# Revit family: MAGIC-HUBLOT_16W_DETECTEUR_1500LM
name_source: partatom
category: Lighting Fixtures
units: mm (PartAtom-declared; Revit-internal decimal feet)

## family parameters
Always vertical = Yes
Cut with Voids When Loaded = No
Host = Ceiling
Light Source = Yes
OmniClass Number = 23.80.70.11
OmniClass Title = Luminaries for Internal Lighting
Part Type = Normal
Room Calculation Point = No
Round Connector Dimension = Use Diameter
Shared = No

## types (1)
- Type 1
    Alimentation = AC 220-240V
    Champs de détection = 180°/360°
    Color Filter = 16777215
    Default Elevation = 0 mm  [stored 0 ft]
    Dimensions = Ø265 x 40 mm
    Dimming Lamp Color Temperature Shift = <None>
    Distance de détection = Mur : 5 à 15m réglable /Plafond : rayon de 2 à 8m réglable
    Durée de vie = 50 000 heures
    Emit Shape Visible in Rendering = No
    Emit from Circle Diameter = 610 mm
    Fintion = Blanc
    IRC = >90
    Lamp = LED SMD
    Maintien du flux = L80B10 (50 000 heures)
    Manufacturer = Lucera - Lucera (c) 06/01/2021 16:38:31 +01:00
    Matériau = Polycarbonate résistant aux UV
    Photometric Web File = google_eulumdat_converter.ies
    Puissance nominale = 16W
    SDCM = <5
    Temporisation = Min 10s à max 12min
    Tilt Angle = 90.00°
    URL = https://www.lucera.fr
    Wattage Comments = 16W

note: [stored X ft] marks values corroborated as IEEE doubles in the binary element streams (Revit-internal decimal feet)

## geometry (parser evidence)
native form markers: Sweep x2
no freeform markers — native parametric forms only
